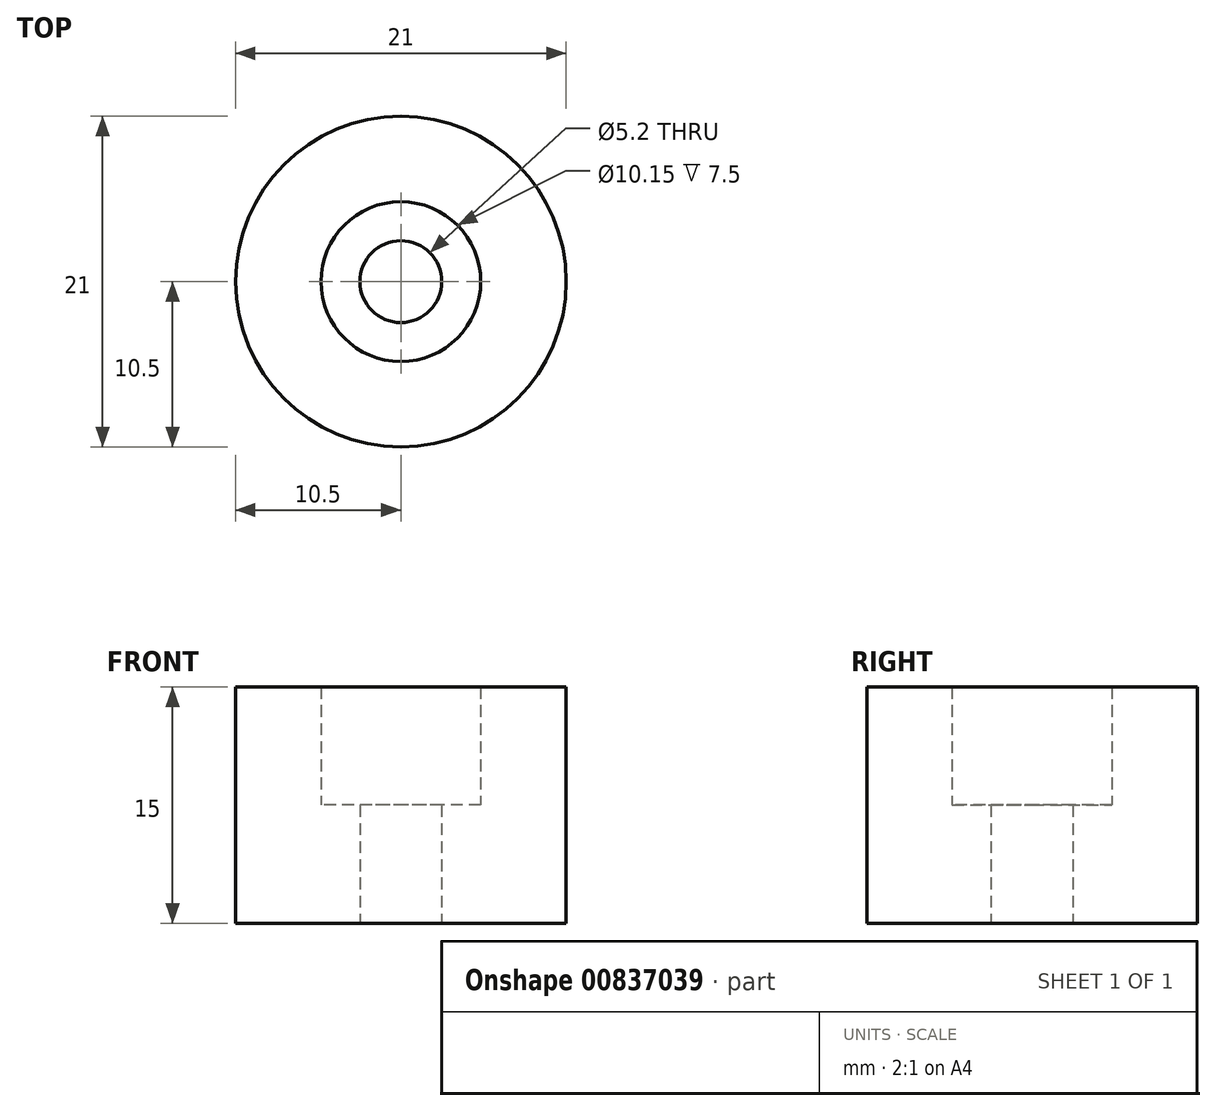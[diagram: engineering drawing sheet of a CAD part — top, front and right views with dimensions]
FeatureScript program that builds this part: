
annotation { "Feature Type Name" : "Feature", "Feature Type Description" : "" }
export const myFeature = defineFeature(function(context is Context, id is Id, definition is map)
    precondition{}
    {
        {
            var Q0;
            Q0=qCreatedBy(makeId("Top.planeOp"),FACE);
            var sketch = newSketch(context, id + "F0", { "sketchPlane" : qUnion([Q0])});
            skCircle(sketch, "E0", {"center": v(0, 0) * mm, "radius": 10.5 * mm});
            skCircle(sketch, "E1", {"center": v(0, 0) * mm, "radius": 2.6 * mm});
            skSolve(sketch);
        }
        {
            var Q0;
            Q0 = qSketchRegion(id + "F0", true);
            extrude(context, id + "F1", {"entities" : qUnion([Q0]), "depth" : 15 * mm, "offsetDistance" : 25 * mm});
        }
        {
            var Q0;
            Q0=qCreatedBy(makeId("Top.planeOp"),FACE);
            var sketch = newSketch(context, id + "F2", { "sketchPlane" : qUnion([Q0])});
            skCircle(sketch, "E2", {"center": v(0, 0) * mm, "radius": 5.08 * mm});
            skSolve(sketch);
        }
        {
            var Q0;
            Q0=makeQuery(id+"F2.imprint","IMPRINT",FACE,{"disambiguationData":[TD([[makeQuery(id+"F2.imprint","IMPRINT",EDGE,{"derivedFrom":sQuery(id+"F2.wireOp",EDGE,"E2")}),1.0]])]});
            extrude(context, id + "F3", {"entities" : qUnion([Q0]), "operationType" : NewBodyOperationType.REMOVE, "depth" : 15 * mm, "offsetDistance" : 25 * mm, "hasSecondDirection" : true, "secondDirectionOppositeDirection" : false, "secondDirectionDepth" : 7.5 * mm});
        }
    });
